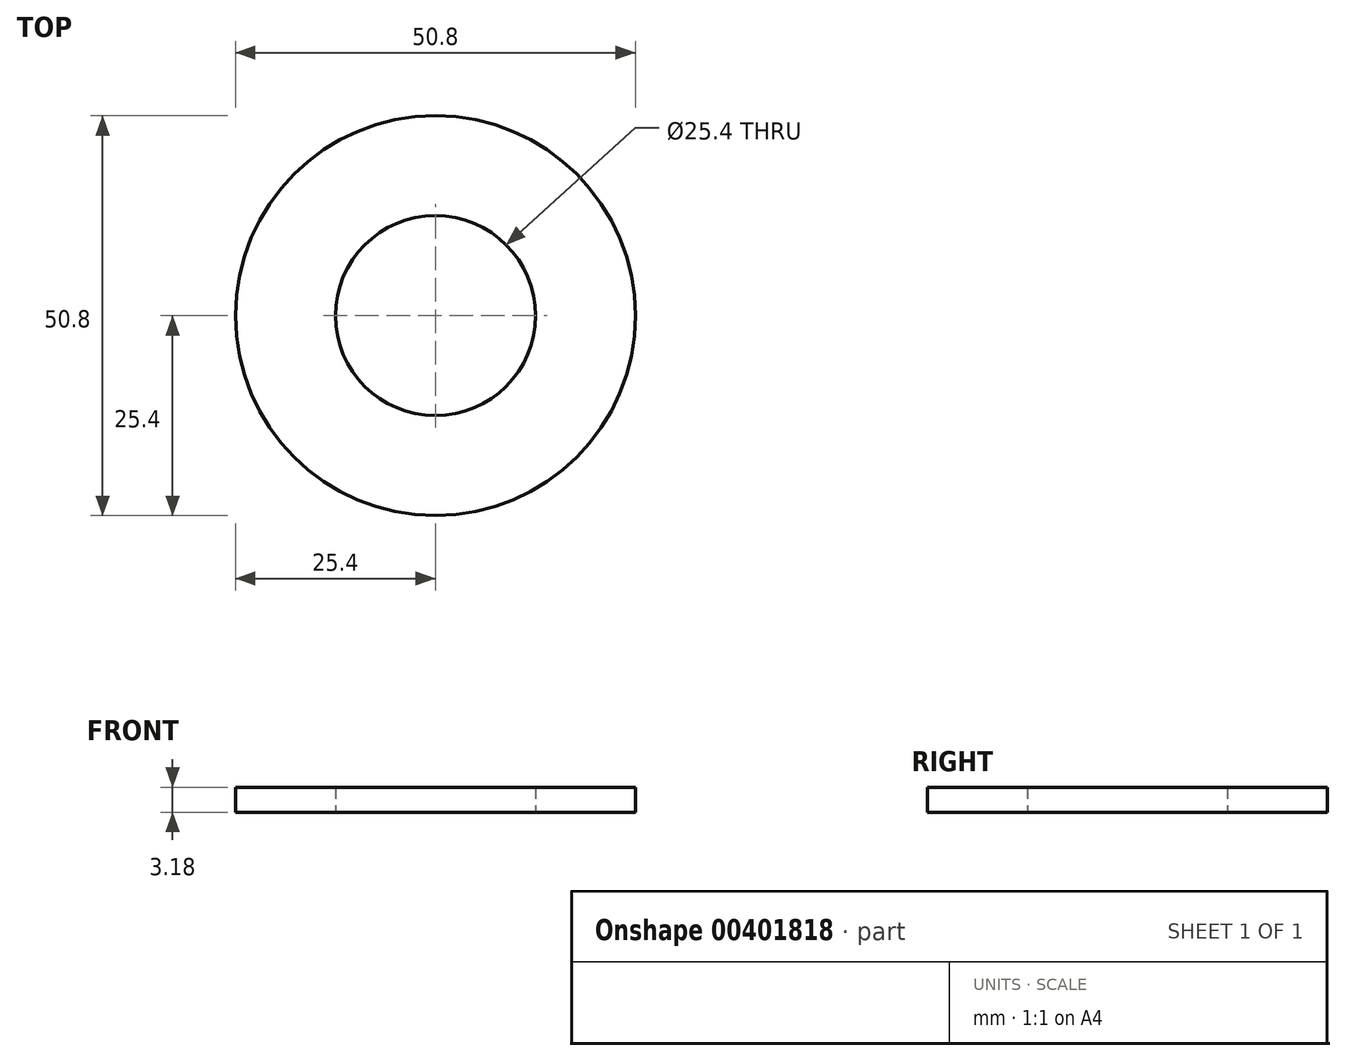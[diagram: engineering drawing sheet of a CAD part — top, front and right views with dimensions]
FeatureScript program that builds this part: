
annotation { "Feature Type Name" : "Feature", "Feature Type Description" : "" }
export const myFeature = defineFeature(function(context is Context, id is Id, definition is map)
    precondition{}
    {
        {
            var Q0;
            Q0=qCreatedBy(makeId("Top.planeOp"),FACE);
            var sketch = newSketch(context, id + "F0", { "sketchPlane" : qUnion([Q0])});
            skCircle(sketch, "E0", {"center": v(0, 0) * mm, "radius": 25.4 * mm});
            skCircle(sketch, "E1", {"center": v(0, 0) * mm, "radius": 12.7 * mm});
            skSolve(sketch);
        }
        {
            var Q0;
            Q0=makeQuery(id+"F0.imprint","IMPRINT",FACE,{"disambiguationData":[TD([[makeQuery(id+"F0.imprint","IMPRINT",EDGE,{"derivedFrom":sQuery(id+"F0.wireOp",EDGE,"E0")}),1.0]])]});
            extrude(context, id + "F1", {"entities" : qUnion([Q0]), "depth" : 3.17 * mm});
        }
    });
